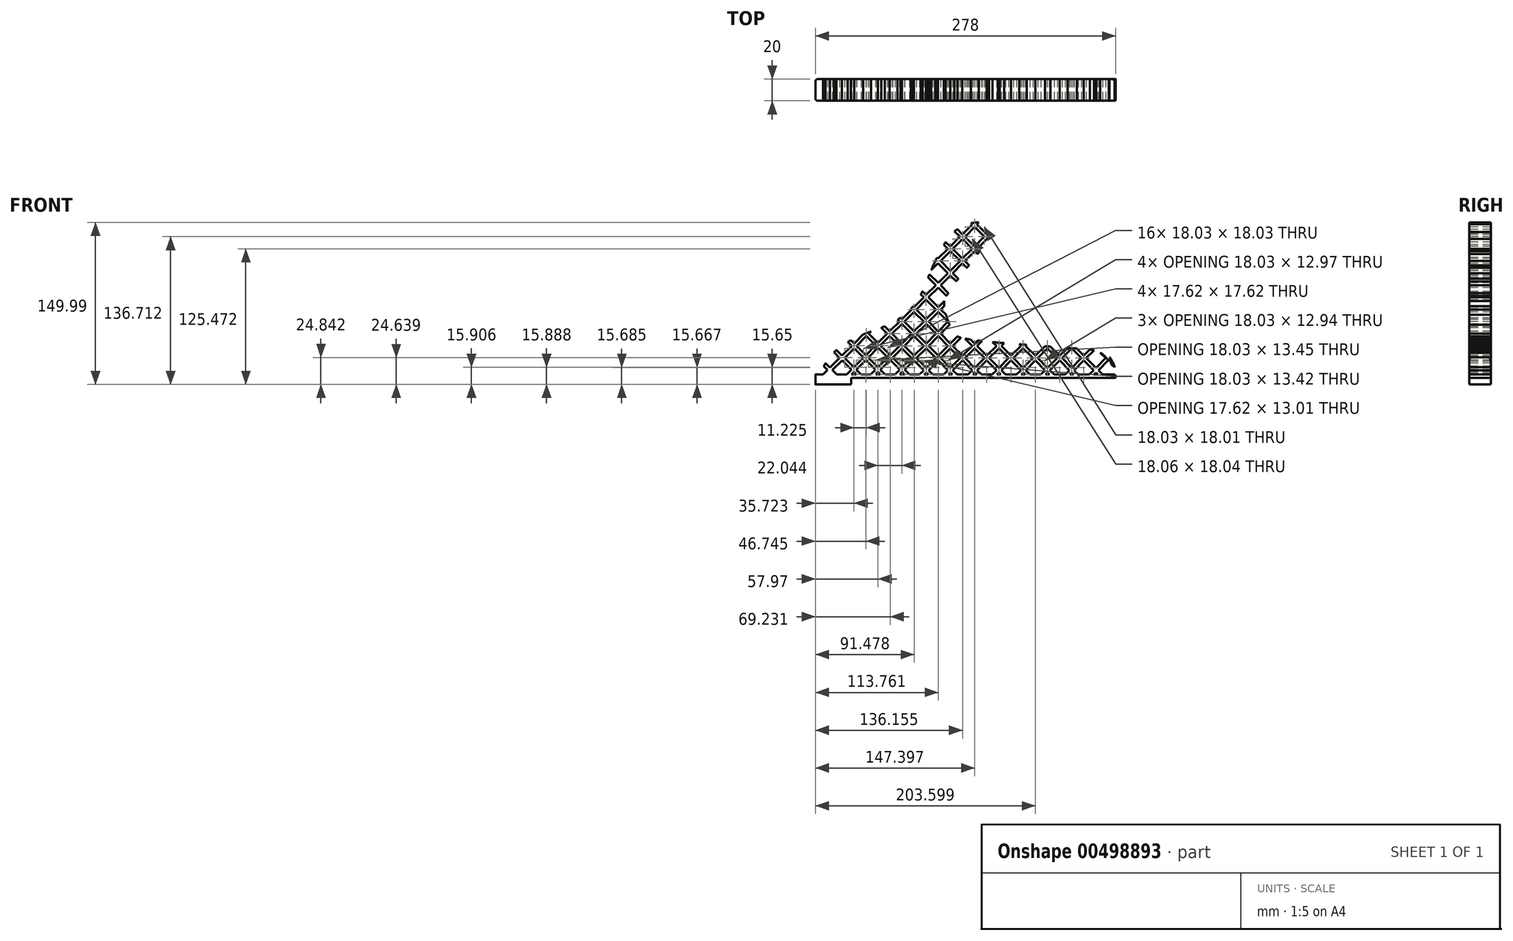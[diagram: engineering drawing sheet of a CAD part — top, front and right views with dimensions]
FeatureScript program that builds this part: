
annotation { "Feature Type Name" : "Feature", "Feature Type Description" : "" }
export const myFeature = defineFeature(function(context is Context, id is Id, definition is map)
    precondition{}
    {
        {
            var Q0;
            Q0=qCreatedBy(makeId("Front.planeOp"),FACE);
            var sketch = newSketch(context, id + "F0", { "sketchPlane" : qUnion([Q0])});
            skLineSegment(sketch, "E0", {"start": v(-83, -3.17) * mm, "end": v(-83, 0) * mm});
            skLineSegment(sketch, "E1", {"start": v(-83, 0) * mm, "end": v(-82.7, 0) * mm});
            skArc(sketch, "E2", {"start": v(162, 0) * mm, "mid": v(155.8, 16.5) * mm, "end": v(140.24, 24.79) * mm});
            skLineSegment(sketch, "E3", {"start": v(140.24, 24.79) * mm, "end": v(39.58, 33.6) * mm});
            skFitSpline(sketch, "E4", {"points": [v(-116, 0) * mm, v(-106.77, 17.97) * mm, v(-86.19, 34.74) * mm, v(-51.87, 47.68) * mm, v(-30.13, 63.36) * mm, v(-15.89, 87.59) * mm, v(-3.25, 115.08) * mm, v(10.46, 133.67) * mm, v(27.88, 142.86) * mm, v(45.91, 140.16) * mm, v(44.88, 124.4) * mm, v(32.37, 105.05) * mm, v(24.04, 94.4) * mm, v(12.3, 78.31) * mm], "startDerivative": vector(110.14, 372.48) * mm, "endDerivative": vector(-175.67, -307.4) * mm});
            skFitSpline(sketch, "E5", {"points": [v(-110.58, 0) * mm, v(-109.72, 3.92) * mm, v(-104.27, 14.22) * mm, v(-97.47, 21.84) * mm, v(-91.58, 26.62) * mm, v(-79.54, 33.6) * mm, v(-68.24, 38.4) * mm, v(-52.26, 44.4) * mm, v(-40.42, 50.4) * mm, v(-31.67, 56.73) * mm, v(-26.67, 61.88) * mm, v(-19.12, 72.72) * mm, v(-10.73, 92.02) * mm, v(-2.47, 110.27) * mm, v(4.52, 122.74) * mm, v(11.8, 131.72) * mm, v(18.12, 135.9) * mm, v(25.92, 139.48) * mm, v(34.7, 140.8) * mm, v(38.92, 140.55) * mm, v(43.31, 138.54) * mm, v(44.78, 133) * mm, v(42.07, 124.02) * mm, v(36.65, 115) * mm, v(29.24, 104.7) * mm, v(18.05, 91.14) * mm, v(10.55, 80.15) * mm, v(5.27, 72.64) * mm, v(3.17, 63.32) * mm, v(10.92, 40.34) * mm, v(22.95, 33.11) * mm, v(135.88, 23.55) * mm, v(145.48, 22.31) * mm, v(155.41, 17.66) * mm, v(158.63, 8.75) * mm, v(163.79, 4.17) * mm, v(158.83, 0) * mm], "startDerivative": vector(86.06, 309.75) * mm, "endDerivative": vector(-2.43, -186.75) * mm});
            skLineSegment(sketch, "E6", {"start": v(-100.7, 0) * mm, "end": v(-102.52, 1.82) * mm});
            skLineSegment(sketch, "E7", {"start": v(-96.29, 0) * mm, "end": v(-100.32, 4.03) * mm});
            skLineSegment(sketch, "E8", {"start": v(-98.81, 20.56) * mm, "end": v(-93.54, 15.3) * mm});
            skLineSegment(sketch, "E9", {"start": v(-96.53, 22.7) * mm, "end": v(-91.33, 17.5) * mm});
            skLineSegment(sketch, "E10", {"start": v(-85.94, 30.14) * mm, "end": v(-82.32, 26.52) * mm});
            skLineSegment(sketch, "E11", {"start": v(-83.11, 31.73) * mm, "end": v(-80.1, 28.73) * mm});
            skLineSegment(sketch, "E12", {"start": v(-68.85, 35.5) * mm, "end": v(-60.24, 26.89) * mm});
            skLineSegment(sketch, "E13", {"start": v(-28.93, 0) * mm, "end": v(-33.33, 4.4) * mm});
            skLineSegment(sketch, "E14", {"start": v(-55.01, 43.3) * mm, "end": v(-49.42, 37.7) * mm});
            skLineSegment(sketch, "E15", {"start": v(-51.87, 44.57) * mm, "end": v(-47.21, 39.92) * mm});
            skLineSegment(sketch, "E16", {"start": v(-39.95, 50.68) * mm, "end": v(-38.2, 48.93) * mm});
            skLineSegment(sketch, "E17", {"start": v(-37.28, 52.44) * mm, "end": v(-35.99, 51.14) * mm});
            skLineSegment(sketch, "E18", {"start": v(-27.6, 60.79) * mm, "end": v(-26.97, 60.16) * mm});
            skLineSegment(sketch, "E19", {"start": v(-25.58, 63.2) * mm, "end": v(-24.76, 62.37) * mm});
            skLineSegment(sketch, "E20", {"start": v(-18.42, 74.05) * mm, "end": v(-15.75, 71.38) * mm});
            skLineSegment(sketch, "E21", {"start": v(-16.97, 77.02) * mm, "end": v(-13.54, 73.6) * mm});
            skLineSegment(sketch, "E22", {"start": v(-11.66, 89.75) * mm, "end": v(-4.52, 82.6) * mm});
            skLineSegment(sketch, "E23", {"start": v(-10.38, 92.89) * mm, "end": v(-2.31, 84.82) * mm});
            skLineSegment(sketch, "E24", {"start": v(-4.84, 105.38) * mm, "end": v(-4.6, 105.15) * mm});
            skLineSegment(sketch, "E25", {"start": v(-3.4, 108.36) * mm, "end": v(-2.4, 107.36) * mm});
            skLineSegment(sketch, "E26", {"start": v(31.39, 114.1) * mm, "end": v(34.18, 111.35) * mm});
            skLineSegment(sketch, "E27", {"start": v(33.6, 116.3) * mm, "end": v(35.96, 113.98) * mm});
            skLineSegment(sketch, "E28", {"start": v(40.41, 127.54) * mm, "end": v(31.38, 136.54) * mm});
            skLineSegment(sketch, "E29", {"start": v(42.62, 129.75) * mm, "end": v(33.32, 139.01) * mm});
            skLineSegment(sketch, "E30", {"start": v(121.27, 24.16) * mm, "end": v(130.3, 15.15) * mm});
            skLineSegment(sketch, "E31", {"start": v(125.87, 24) * mm, "end": v(132.5, 17.36) * mm});
            skLineSegment(sketch, "E32.trimOffspring", {"start": v(101.57, 25.84) * mm, "end": v(110.05, 17.36) * mm});
            skLineSegment(sketch, "E33.trimOffspring", {"start": v(98.82, 24.16) * mm, "end": v(107.84, 15.15) * mm});
            skLineSegment(sketch, "E34.trimOffspring", {"start": v(78.55, 26.4) * mm, "end": v(87.56, 17.4) * mm});
            skLineSegment(sketch, "E35.trimOffspring", {"start": v(72.62, 27.92) * mm, "end": v(74.13, 26.4) * mm});
            skLineSegment(sketch, "E36.trimOffspring", {"start": v(52.95, 29.56) * mm, "end": v(53.77, 28.74) * mm});
            skLineSegment(sketch, "E37.trimOffspring", {"start": v(48.08, 30) * mm, "end": v(51.68, 26.4) * mm});
            skLineSegment(sketch, "E38", {"start": v(-104.34, 0) * mm, "end": v(-102.52, 1.82) * mm});
            skLineSegment(sketch, "E39", {"start": v(-108.83, 0) * mm, "end": v(-104.77, 4.07) * mm});
            skLineSegment(sketch, "E40", {"start": v(-87.13, 0) * mm, "end": v(-82.7, 4.44) * mm});
            skLineSegment(sketch, "E41.trimOffspring", {"start": v(42.62, 129.75) * mm, "end": v(44.65, 131.77) * mm});
            skLineSegment(sketch, "E42", {"start": v(-82.7, 0) * mm, "end": v(-80.48, 2.23) * mm});
            skLineSegment(sketch, "E43", {"start": v(-5.25, 104.5) * mm, "end": v(-4.6, 105.15) * mm});
            skLineSegment(sketch, "E44", {"start": v(20.08, 129.63) * mm, "end": v(29.08, 138.66) * mm});
            skLineSegment(sketch, "E45.trimOffspring", {"start": v(29.08, 138.66) * mm, "end": v(27.78, 139.96) * mm});
            skLineSegment(sketch, "E46.trimOffspring", {"start": v(33.32, 139.01) * mm, "end": v(35.11, 140.81) * mm});
            skLineSegment(sketch, "E47", {"start": v(-60.19, 0) * mm, "end": v(-58, 2.2) * mm});
            skLineSegment(sketch, "E48", {"start": v(-64.68, 0) * mm, "end": v(-60.24, 4.44) * mm});
            skLineSegment(sketch, "E49", {"start": v(-42.15, 0) * mm, "end": v(-37.75, 4.4) * mm});
            skLineSegment(sketch, "E50", {"start": v(-37.74, 0) * mm, "end": v(-35.54, 2.2) * mm});
            skLineSegment(sketch, "E51", {"start": v(-15.21, 0) * mm, "end": v(-13.46, 1.75) * mm});
            skLineSegment(sketch, "E52", {"start": v(-19.7, 0) * mm, "end": v(-15.7, 4) * mm});
            skLineSegment(sketch, "E53", {"start": v(2.82, 0) * mm, "end": v(6.78, 3.96) * mm});
            skLineSegment(sketch, "E54", {"start": v(7.24, 0) * mm, "end": v(8.99, 1.75) * mm});
            skLineSegment(sketch, "E55", {"start": v(29.69, 0) * mm, "end": v(31.44, 1.75) * mm});
            skLineSegment(sketch, "E56", {"start": v(25.27, 0) * mm, "end": v(29.23, 3.96) * mm});
            skLineSegment(sketch, "E57", {"start": v(47.72, 0) * mm, "end": v(51.68, 3.96) * mm});
            skLineSegment(sketch, "E58", {"start": v(52.14, 0) * mm, "end": v(53.89, 1.75) * mm});
            skLineSegment(sketch, "E59", {"start": v(74.66, 0) * mm, "end": v(76.37, 1.71) * mm});
            skLineSegment(sketch, "E60", {"start": v(70.17, 0) * mm, "end": v(74.13, 3.96) * mm});
            skLineSegment(sketch, "E61", {"start": v(92.7, 0) * mm, "end": v(96.61, 3.92) * mm});
            skLineSegment(sketch, "E62", {"start": v(97.1, 0) * mm, "end": v(98.82, 1.71) * mm});
            skLineSegment(sketch, "E63", {"start": v(119.56, 0) * mm, "end": v(121.27, 1.71) * mm});
            skLineSegment(sketch, "E64", {"start": v(115.14, 0) * mm, "end": v(119.06, 3.92) * mm});
            skLineSegment(sketch, "E65", {"start": v(137.6, 0) * mm, "end": v(141.52, 3.92) * mm});
            skLineSegment(sketch, "E66", {"start": v(142.01, 0) * mm, "end": v(143.73, 1.71) * mm});
            skPoint(sketch, "E67.orphan", {"position": v(103.07, -34.52) * mm});
            skPoint(sketch, "E68.orphan", {"position": v(85.04, -34.52) * mm});
            skPoint(sketch, "E69.orphan", {"position": v(0, -2.82) * mm});
            skLineSegment(sketch, "E70", {"start": v(-83, 0) * mm, "end": v(-100.7, 0) * mm});
            skLineSegment(sketch, "E71.trimOffspring", {"start": v(-104.77, 4.07) * mm, "end": v(-108.22, 7.52) * mm});
            skLineSegment(sketch, "E72.trimOffspring", {"start": v(-102.56, 6.27) * mm, "end": v(-93.54, 15.3) * mm});
            skLineSegment(sketch, "E73.trimOffspring", {"start": v(-102.56, 6.27) * mm, "end": v(-106.68, 10.4) * mm});
            skLineSegment(sketch, "E74.trimOffspring", {"start": v(-100.32, 4.03) * mm, "end": v(-91.3, 13.05) * mm});
            skLineSegment(sketch, "E75.trimOffspring", {"start": v(-91.3, 13.05) * mm, "end": v(-82.7, 4.44) * mm});
            skLineSegment(sketch, "E76.trimOffspring", {"start": v(-89.09, 15.26) * mm, "end": v(-80.48, 6.65) * mm});
            skLineSegment(sketch, "E77.trimOffspring", {"start": v(-91.33, 17.5) * mm, "end": v(-82.32, 26.52) * mm});
            skLineSegment(sketch, "E78.trimOffspring", {"start": v(-89.09, 15.26) * mm, "end": v(-80.07, 24.27) * mm});
            skLineSegment(sketch, "E79.trimOffspring", {"start": v(-80.48, 6.65) * mm, "end": v(-71.47, 15.66) * mm});
            skLineSegment(sketch, "E80.trimOffspring", {"start": v(-78.27, 4.44) * mm, "end": v(-69.26, 13.45) * mm});
            skLineSegment(sketch, "E81.trimOffspring", {"start": v(-78.27, 4.44) * mm, "end": v(-73.83, 0) * mm});
            skLineSegment(sketch, "E82.trimOffspring", {"start": v(-80.48, 2.23) * mm, "end": v(-78.25, 0) * mm});
            skLineSegment(sketch, "E83.trimOffspring", {"start": v(-80.07, 24.27) * mm, "end": v(-71.47, 15.66) * mm});
            skLineSegment(sketch, "E84.trimOffspring", {"start": v(-77.86, 26.48) * mm, "end": v(-69.26, 17.87) * mm});
            skLineSegment(sketch, "E85.trimOffspring", {"start": v(-80.1, 28.73) * mm, "end": v(-71.8, 37.04) * mm});
            skLineSegment(sketch, "E86.trimOffspring", {"start": v(-77.86, 26.48) * mm, "end": v(-68.85, 35.5) * mm});
            skLineSegment(sketch, "E87.trimOffspring", {"start": v(-69.26, 17.87) * mm, "end": v(-60.24, 26.89) * mm});
            skLineSegment(sketch, "E88.trimOffspring", {"start": v(-67.05, 15.66) * mm, "end": v(-58.03, 24.68) * mm});
            skLineSegment(sketch, "E89.trimOffspring", {"start": v(-67.05, 15.66) * mm, "end": v(-58.03, 6.65) * mm});
            skLineSegment(sketch, "E90.trimOffspring", {"start": v(-69.26, 13.45) * mm, "end": v(-60.24, 4.44) * mm});
            skLineSegment(sketch, "E91.trimOffspring", {"start": v(-58, 2.2) * mm, "end": v(-55.8, 0) * mm});
            skLineSegment(sketch, "E92.trimOffspring", {"start": v(-58.03, 6.65) * mm, "end": v(-49.01, 15.66) * mm});
            skLineSegment(sketch, "E93.trimOffspring", {"start": v(-55.78, 4.4) * mm, "end": v(-51.38, 0) * mm});
            skLineSegment(sketch, "E94.trimOffspring", {"start": v(-55.78, 4.4) * mm, "end": v(-46.77, 13.42) * mm});
            skLineSegment(sketch, "E95.trimOffspring", {"start": v(-66.64, 37.7) * mm, "end": v(-64.61, 39.73) * mm});
            skLineSegment(sketch, "E96.trimOffspring", {"start": v(-58.03, 29.1) * mm, "end": v(-49.42, 37.7) * mm});
            skLineSegment(sketch, "E97.trimOffspring", {"start": v(-55.82, 26.89) * mm, "end": v(-47.21, 35.5) * mm});
            skLineSegment(sketch, "E98.trimOffspring", {"start": v(-58.03, 29.1) * mm, "end": v(-66.64, 37.7) * mm});
            skLineSegment(sketch, "E99.trimOffspring", {"start": v(-58.03, 24.68) * mm, "end": v(-49.01, 15.66) * mm});
            skLineSegment(sketch, "E100.trimOffspring", {"start": v(-46.8, 17.87) * mm, "end": v(-38.2, 26.48) * mm});
            skLineSegment(sketch, "E101.trimOffspring", {"start": v(-44.56, 15.63) * mm, "end": v(-35.95, 24.24) * mm});
            skLineSegment(sketch, "E102.trimOffspring", {"start": v(-46.8, 17.87) * mm, "end": v(-55.82, 26.89) * mm});
            skLineSegment(sketch, "E103.trimOffspring", {"start": v(-46.77, 13.42) * mm, "end": v(-37.75, 4.4) * mm});
            skLineSegment(sketch, "E104.trimOffspring", {"start": v(-47.21, 39.92) * mm, "end": v(-38.2, 48.93) * mm});
            skLineSegment(sketch, "E105.trimOffspring", {"start": v(-45, 37.7) * mm, "end": v(-35.99, 28.7) * mm});
            skLineSegment(sketch, "E106.trimOffspring", {"start": v(-47.21, 35.5) * mm, "end": v(-38.2, 26.48) * mm});
            skLineSegment(sketch, "E107.trimOffspring", {"start": v(-45, 37.7) * mm, "end": v(-35.99, 46.72) * mm});
            skLineSegment(sketch, "E108.trimOffspring", {"start": v(-35.99, 28.7) * mm, "end": v(-26.97, 37.7) * mm});
            skLineSegment(sketch, "E109.trimOffspring", {"start": v(-33.74, 26.45) * mm, "end": v(-24.73, 35.46) * mm});
            skLineSegment(sketch, "E110.trimOffspring", {"start": v(-33.74, 26.45) * mm, "end": v(-24.73, 17.43) * mm});
            skLineSegment(sketch, "E111.trimOffspring", {"start": v(-35.95, 24.24) * mm, "end": v(-26.94, 15.22) * mm});
            skLineSegment(sketch, "E112.trimOffspring", {"start": v(-35.99, 46.72) * mm, "end": v(-26.97, 37.7) * mm});
            skLineSegment(sketch, "E113.trimOffspring", {"start": v(-35.99, 51.14) * mm, "end": v(-26.97, 60.16) * mm});
            skLineSegment(sketch, "E114.trimOffspring", {"start": v(-33.78, 48.93) * mm, "end": v(-24.76, 39.92) * mm});
            skLineSegment(sketch, "E115.trimOffspring", {"start": v(-33.78, 48.93) * mm, "end": v(-24.76, 57.95) * mm});
            skLineSegment(sketch, "E116.trimOffspring", {"start": v(-24.76, 39.92) * mm, "end": v(-15.75, 48.93) * mm});
            skLineSegment(sketch, "E117.trimOffspring", {"start": v(-22.52, 37.67) * mm, "end": v(-13.5, 46.69) * mm});
            skLineSegment(sketch, "E118.trimOffspring", {"start": v(-22.52, 37.67) * mm, "end": v(-13.5, 28.65) * mm});
            skLineSegment(sketch, "E119.trimOffspring", {"start": v(-24.73, 35.46) * mm, "end": v(-15.7, 26.45) * mm});
            skLineSegment(sketch, "E120.trimOffspring", {"start": v(-24.73, 17.43) * mm, "end": v(-15.7, 26.45) * mm});
            skLineSegment(sketch, "E121.trimOffspring", {"start": v(-22.52, 15.22) * mm, "end": v(-13.5, 24.24) * mm});
            skLineSegment(sketch, "E122.trimOffspring", {"start": v(-22.52, 15.22) * mm, "end": v(-13.5, 6.2) * mm});
            skLineSegment(sketch, "E123.trimOffspring", {"start": v(-24.73, 13.01) * mm, "end": v(-15.7, 4) * mm});
            skLineSegment(sketch, "E124.trimOffspring", {"start": v(-35.54, 6.61) * mm, "end": v(-44.56, 15.63) * mm});
            skLineSegment(sketch, "E125.trimOffspring", {"start": v(-35.54, 6.61) * mm, "end": v(-26.94, 15.22) * mm});
            skLineSegment(sketch, "E126.trimOffspring", {"start": v(-35.54, 2.2) * mm, "end": v(-33.35, 0) * mm});
            skLineSegment(sketch, "E127.trimOffspring", {"start": v(-33.33, 4.4) * mm, "end": v(-24.73, 13.01) * mm});
            skLineSegment(sketch, "E128.trimOffspring", {"start": v(-13.5, 6.2) * mm, "end": v(-4.48, 15.22) * mm});
            skLineSegment(sketch, "E129.trimOffspring", {"start": v(-11.25, 3.96) * mm, "end": v(-2.24, 12.97) * mm});
            skLineSegment(sketch, "E130.trimOffspring", {"start": v(-13.46, 1.75) * mm, "end": v(-11.72, 0) * mm});
            skLineSegment(sketch, "E131.trimOffspring", {"start": v(-11.25, 3.96) * mm, "end": v(-7.3, 0) * mm});
            skLineSegment(sketch, "E132.trimOffspring", {"start": v(-2.27, 17.43) * mm, "end": v(6.74, 26.45) * mm});
            skLineSegment(sketch, "E133.trimOffspring", {"start": v(-0.03, 15.18) * mm, "end": v(8.99, 24.2) * mm});
            skLineSegment(sketch, "E134.trimOffspring", {"start": v(-2.24, 12.97) * mm, "end": v(6.78, 3.96) * mm});
            skLineSegment(sketch, "E135.trimOffspring", {"start": v(-0.03, 15.18) * mm, "end": v(8.99, 6.17) * mm});
            skLineSegment(sketch, "E136.trimOffspring", {"start": v(-11.3, 26.45) * mm, "end": v(-2.27, 17.43) * mm});
            skLineSegment(sketch, "E137.trimOffspring", {"start": v(-13.5, 24.24) * mm, "end": v(-4.48, 15.22) * mm});
            skLineSegment(sketch, "E138.trimOffspring", {"start": v(-13.5, 28.65) * mm, "end": v(-4.48, 37.67) * mm});
            skLineSegment(sketch, "E139.trimOffspring", {"start": v(-11.3, 26.45) * mm, "end": v(-2.27, 35.46) * mm});
            skLineSegment(sketch, "E140.trimOffspring", {"start": v(-24.76, 57.95) * mm, "end": v(-15.75, 48.93) * mm});
            skLineSegment(sketch, "E141.trimOffspring", {"start": v(-24.76, 62.37) * mm, "end": v(-15.75, 71.38) * mm});
            skLineSegment(sketch, "E142.trimOffspring", {"start": v(-22.55, 60.16) * mm, "end": v(-13.54, 51.14) * mm});
            skLineSegment(sketch, "E143.trimOffspring", {"start": v(-22.55, 60.16) * mm, "end": v(-13.54, 69.17) * mm});
            skLineSegment(sketch, "E144.trimOffspring", {"start": v(-13.54, 69.17) * mm, "end": v(-4.52, 60.16) * mm});
            skLineSegment(sketch, "E145.trimOffspring", {"start": v(-13.54, 73.6) * mm, "end": v(-4.52, 82.6) * mm});
            skLineSegment(sketch, "E146.trimOffspring", {"start": v(-11.33, 71.38) * mm, "end": v(-2.27, 62.33) * mm});
            skLineSegment(sketch, "E147.trimOffspring", {"start": v(-11.33, 71.38) * mm, "end": v(-2.31, 80.4) * mm});
            skLineSegment(sketch, "E148.trimOffspring", {"start": v(-0.06, 60.12) * mm, "end": v(8.95, 69.14) * mm});
            skLineSegment(sketch, "E149.trimOffspring", {"start": v(-2.27, 57.91) * mm, "end": v(6.74, 48.9) * mm});
            skLineSegment(sketch, "E150.trimOffspring", {"start": v(-11.3, 48.9) * mm, "end": v(-2.27, 39.88) * mm});
            skLineSegment(sketch, "E151.trimOffspring", {"start": v(-13.54, 51.14) * mm, "end": v(-4.52, 60.16) * mm});
            skLineSegment(sketch, "E152.trimOffspring", {"start": v(-13.5, 46.69) * mm, "end": v(-4.48, 37.67) * mm});
            skLineSegment(sketch, "E153.trimOffspring", {"start": v(-11.3, 48.9) * mm, "end": v(-2.27, 57.91) * mm});
            skLineSegment(sketch, "E154.trimOffspring", {"start": v(-2.27, 39.88) * mm, "end": v(6.74, 48.9) * mm});
            skLineSegment(sketch, "E155.trimOffspring", {"start": v(-0.06, 37.67) * mm, "end": v(8.99, 28.62) * mm});
            skLineSegment(sketch, "E156.trimOffspring", {"start": v(-2.27, 35.46) * mm, "end": v(6.74, 26.45) * mm});
            skLineSegment(sketch, "E157.trimOffspring", {"start": v(22.5, 15.27) * mm, "end": v(31.44, 24.2) * mm});
            skLineSegment(sketch, "E158.trimOffspring", {"start": v(8.99, 24.2) * mm, "end": v(18, 15.18) * mm});
            skLineSegment(sketch, "E159.trimOffspring", {"start": v(20.21, 12.97) * mm, "end": v(29.23, 3.96) * mm});
            skLineSegment(sketch, "E160.trimOffspring", {"start": v(22.42, 15.18) * mm, "end": v(31.44, 6.17) * mm});
            skLineSegment(sketch, "E161.trimOffspring", {"start": v(20.21, 17.4) * mm, "end": v(29.23, 26.4) * mm});
            skLineSegment(sketch, "E162.trimOffspring", {"start": v(22.42, 15.18) * mm, "end": v(31.44, 24.2) * mm});
            skLineSegment(sketch, "E163.trimOffspring", {"start": v(31.44, 24.2) * mm, "end": v(40.45, 15.18) * mm});
            skLineSegment(sketch, "E164.trimOffspring", {"start": v(33.65, 26.4) * mm, "end": v(42.66, 17.4) * mm});
            skLineSegment(sketch, "E165.trimOffspring", {"start": v(33.65, 26.4) * mm, "end": v(38.25, 31.02) * mm});
            skLineSegment(sketch, "E166.trimOffspring", {"start": v(44.87, 15.18) * mm, "end": v(53.89, 6.17) * mm});
            skLineSegment(sketch, "E167.trimOffspring", {"start": v(42.66, 12.97) * mm, "end": v(51.68, 3.96) * mm});
            skLineSegment(sketch, "E168.trimOffspring", {"start": v(44.87, 15.18) * mm, "end": v(53.89, 24.2) * mm});
            skLineSegment(sketch, "E169.trimOffspring", {"start": v(53.89, 24.2) * mm, "end": v(62.9, 15.18) * mm});
            skLineSegment(sketch, "E170.trimOffspring", {"start": v(56.1, 26.4) * mm, "end": v(65.11, 17.4) * mm});
            skLineSegment(sketch, "E171.trimOffspring", {"start": v(53.77, 28.74) * mm, "end": v(54.45, 29.42) * mm});
            skLineSegment(sketch, "E172.trimOffspring", {"start": v(56.1, 26.4) * mm, "end": v(58.73, 29.05) * mm});
            skLineSegment(sketch, "E173.trimOffspring", {"start": v(56.1, 3.96) * mm, "end": v(60.06, 0) * mm});
            skLineSegment(sketch, "E174.trimOffspring", {"start": v(53.89, 6.17) * mm, "end": v(62.9, 15.18) * mm});
            skLineSegment(sketch, "E175.trimOffspring", {"start": v(53.89, 1.75) * mm, "end": v(55.64, 0) * mm});
            skLineSegment(sketch, "E176.trimOffspring", {"start": v(56.1, 3.96) * mm, "end": v(65.11, 12.97) * mm});
            skLineSegment(sketch, "E177.trimOffspring", {"start": v(65.11, 17.4) * mm, "end": v(74.13, 26.4) * mm});
            skLineSegment(sketch, "E178.trimOffspring", {"start": v(67.32, 15.18) * mm, "end": v(76.34, 6.17) * mm});
            skLineSegment(sketch, "E179.trimOffspring", {"start": v(67.32, 15.18) * mm, "end": v(76.34, 24.2) * mm});
            skLineSegment(sketch, "E180.trimOffspring", {"start": v(65.11, 12.97) * mm, "end": v(74.13, 3.96) * mm});
            skLineSegment(sketch, "E181.trimOffspring", {"start": v(76.34, 6.17) * mm, "end": v(85.35, 15.18) * mm});
            skLineSegment(sketch, "E182.trimOffspring", {"start": v(78.58, 3.92) * mm, "end": v(82.5, 0) * mm});
            skLineSegment(sketch, "E183.trimOffspring", {"start": v(76.37, 1.71) * mm, "end": v(78.09, 0) * mm});
            skLineSegment(sketch, "E184.trimOffspring", {"start": v(78.58, 3.92) * mm, "end": v(87.6, 12.94) * mm});
            skLineSegment(sketch, "E185.trimOffspring", {"start": v(87.6, 12.94) * mm, "end": v(96.61, 3.92) * mm});
            skLineSegment(sketch, "E186.trimOffspring", {"start": v(78.55, 26.4) * mm, "end": v(79.53, 27.4) * mm});
            skLineSegment(sketch, "E187.trimOffspring", {"start": v(76.34, 24.2) * mm, "end": v(85.35, 15.18) * mm});
            skLineSegment(sketch, "E188.trimOffspring", {"start": v(89.8, 15.15) * mm, "end": v(98.82, 24.16) * mm});
            skLineSegment(sketch, "E189.trimOffspring", {"start": v(89.8, 15.15) * mm, "end": v(98.82, 6.13) * mm});
            skLineSegment(sketch, "E190.trimOffspring", {"start": v(87.56, 17.4) * mm, "end": v(96.36, 26.2) * mm});
            skLineSegment(sketch, "E191.trimOffspring", {"start": v(110.05, 17.36) * mm, "end": v(117.32, 24.63) * mm});
            skLineSegment(sketch, "E192.trimOffspring", {"start": v(112.26, 15.15) * mm, "end": v(121.27, 6.13) * mm});
            skLineSegment(sketch, "E193.trimOffspring", {"start": v(112.26, 15.15) * mm, "end": v(121.27, 24.16) * mm});
            skLineSegment(sketch, "E194.trimOffspring", {"start": v(110.05, 12.94) * mm, "end": v(119.06, 3.92) * mm});
            skLineSegment(sketch, "E195.trimOffspring", {"start": v(101.03, 3.92) * mm, "end": v(104.96, 0) * mm});
            skLineSegment(sketch, "E196.trimOffspring", {"start": v(98.82, 6.13) * mm, "end": v(107.84, 15.15) * mm});
            skLineSegment(sketch, "E197.trimOffspring", {"start": v(98.82, 1.71) * mm, "end": v(100.54, 0) * mm});
            skLineSegment(sketch, "E198.trimOffspring", {"start": v(101.03, 3.92) * mm, "end": v(110.05, 12.94) * mm});
            skLineSegment(sketch, "E199.trimOffspring", {"start": v(132.5, 17.36) * mm, "end": v(138.23, 23.1) * mm});
            skLineSegment(sketch, "E200.trimOffspring", {"start": v(134.7, 15.15) * mm, "end": v(141.93, 22.37) * mm});
            skLineSegment(sketch, "E201.trimOffspring", {"start": v(134.7, 15.15) * mm, "end": v(143.73, 6.13) * mm});
            skLineSegment(sketch, "E202.trimOffspring", {"start": v(132.5, 12.94) * mm, "end": v(141.52, 3.92) * mm});
            skLineSegment(sketch, "E203.trimOffspring", {"start": v(123.48, 3.92) * mm, "end": v(127.4, 0) * mm});
            skLineSegment(sketch, "E204.trimOffspring", {"start": v(121.27, 1.71) * mm, "end": v(122.99, 0) * mm});
            skLineSegment(sketch, "E205.trimOffspring", {"start": v(121.27, 6.13) * mm, "end": v(130.3, 15.15) * mm});
            skLineSegment(sketch, "E206.trimOffspring", {"start": v(123.48, 3.92) * mm, "end": v(132.5, 12.94) * mm});
            skLineSegment(sketch, "E207.trimOffspring", {"start": v(143.73, 6.13) * mm, "end": v(152.74, 15.15) * mm});
            skLineSegment(sketch, "E208.trimOffspring", {"start": v(145.93, 3.92) * mm, "end": v(154.95, 12.94) * mm});
            skLineSegment(sketch, "E209.trimOffspring", {"start": v(145.93, 3.92) * mm, "end": v(149.86, 0) * mm});
            skLineSegment(sketch, "E210.trimOffspring", {"start": v(143.73, 1.71) * mm, "end": v(145.44, 0) * mm});
            skLineSegment(sketch, "E211.trimOffspring", {"start": v(-2.31, 84.82) * mm, "end": v(6.7, 93.83) * mm});
            skLineSegment(sketch, "E212.trimOffspring", {"start": v(-0.1, 82.6) * mm, "end": v(8.92, 91.62) * mm});
            skLineSegment(sketch, "E213.trimOffspring", {"start": v(-2.4, 107.36) * mm, "end": v(6.54, 116.3) * mm});
            skLineSegment(sketch, "E214.trimOffspring", {"start": v(-2.4, 102.94) * mm, "end": v(6.7, 93.83) * mm});
            skLineSegment(sketch, "E215.trimOffspring", {"start": v(-0.1, 105.06) * mm, "end": v(8.91, 114.08) * mm});
            skLineSegment(sketch, "E216.trimOffspring", {"start": v(6.54, 116.3) * mm, "end": v(2.82, 120.02) * mm});
            skLineSegment(sketch, "E217.trimOffspring", {"start": v(8.75, 118.5) * mm, "end": v(17.77, 127.52) * mm});
            skLineSegment(sketch, "E218.trimOffspring", {"start": v(8.75, 118.5) * mm, "end": v(4.52, 122.74) * mm});
            skLineSegment(sketch, "E219.trimOffspring", {"start": v(11.12, 116.29) * mm, "end": v(20.15, 125.31) * mm});
            skLineSegment(sketch, "E220.trimOffspring", {"start": v(17.93, 105.06) * mm, "end": v(8.91, 114.08) * mm});
            skLineSegment(sketch, "E221.trimOffspring", {"start": v(22.37, 105.08) * mm, "end": v(31.39, 114.1) * mm});
            skLineSegment(sketch, "E222.trimOffspring", {"start": v(20.14, 107.27) * mm, "end": v(11.12, 116.29) * mm});
            skLineSegment(sketch, "E223.trimOffspring", {"start": v(29.19, 116.32) * mm, "end": v(20.15, 125.31) * mm});
            skLineSegment(sketch, "E224.trimOffspring", {"start": v(31.4, 118.52) * mm, "end": v(22.38, 127.5) * mm});
            skLineSegment(sketch, "E225.trimOffspring", {"start": v(33.6, 116.3) * mm, "end": v(42.7, 125.42) * mm});
            skLineSegment(sketch, "E226.trimOffspring", {"start": v(31.4, 118.52) * mm, "end": v(40.41, 127.54) * mm});
            skLineSegment(sketch, "E227.trimOffspring", {"start": v(22.38, 127.5) * mm, "end": v(31.38, 136.54) * mm});
            skLineSegment(sketch, "E228.trimOffspring", {"start": v(17.77, 127.52) * mm, "end": v(12.76, 132.53) * mm});
            skLineSegment(sketch, "E229.trimOffspring", {"start": v(20.08, 129.63) * mm, "end": v(15.37, 134.34) * mm});
            skLineSegment(sketch, "E230.trimOffspring", {"start": v(20.14, 107.27) * mm, "end": v(29.19, 116.32) * mm});
            skLineSegment(sketch, "E231.trimOffspring", {"start": v(-104.34, 0) * mm, "end": v(-116, 0) * mm});
            skLineSegment(sketch, "E232.trimOffspring", {"start": v(-78.25, 0) * mm, "end": v(159.43, 0) * mm});
            skLineSegment(sketch, "E233", {"start": v(-82.7, 0) * mm, "end": v(-78.25, 0) * mm});
            skLineSegment(sketch, "E234.trimOffspring", {"start": v(31.44, 6.17) * mm, "end": v(40.45, 15.18) * mm});
            skLineSegment(sketch, "E235.trimOffspring", {"start": v(33.65, 3.96) * mm, "end": v(42.66, 12.97) * mm});
            skLineSegment(sketch, "E236.trimOffspring", {"start": v(31.44, 1.75) * mm, "end": v(33.19, 0) * mm});
            skLineSegment(sketch, "E237.trimOffspring", {"start": v(33.65, 3.96) * mm, "end": v(37.6, 0) * mm});
            skLineSegment(sketch, "E238.trimOffspring", {"start": v(11.2, 3.96) * mm, "end": v(15.15, 0) * mm});
            skLineSegment(sketch, "E239.trimOffspring", {"start": v(8.99, 6.17) * mm, "end": v(18, 15.18) * mm});
            skLineSegment(sketch, "E240.trimOffspring", {"start": v(8.99, 1.75) * mm, "end": v(10.74, 0) * mm});
            skLineSegment(sketch, "E241.trimOffspring", {"start": v(11.2, 3.96) * mm, "end": v(20.21, 12.97) * mm});
            skFitSpline(sketch, "E242", {"points": [v(39.58, 33.6) * mm, v(29.2, 36.2) * mm, v(24.64, 38.85) * mm, v(19.31, 45.16) * mm, v(16.43, 50.98) * mm, v(15.23, 59.34) * mm, v(15.57, 67.86) * mm, v(16.67, 75.73) * mm, v(18.02, 81.55) * mm, v(20.18, 87.66) * mm, v(24.04, 94.4) * mm], "startDerivative": vector(-99.51, 16.75) * mm, "endDerivative": vector(46.52, 71.35) * mm});
            skFitSpline(sketch, "E243", {"points": [v(38.25, 31.02) * mm, v(27.62, 33.52) * mm, v(22.42, 37.1) * mm, v(17.07, 43.11) * mm, v(14.09, 49.32) * mm, v(12.87, 58.46) * mm, v(12.92, 67) * mm, v(13.91, 74.62) * mm, v(15.42, 81.11) * mm, v(17.59, 88.06) * mm, v(21.9, 95.95) * mm], "startDerivative": vector(-99.47, 17.06) * mm, "endDerivative": vector(46.53, 71.34) * mm});
            skLineSegment(sketch, "E244", {"start": v(8.99, 28.62) * mm, "end": v(18, 37.64) * mm});
            skLineSegment(sketch, "E245", {"start": v(20.21, 17.4) * mm, "end": v(11.2, 26.4) * mm});
            skLineSegment(sketch, "E246", {"start": v(11.2, 26.4) * mm, "end": v(20.21, 35.43) * mm});
            skLineSegment(sketch, "E247", {"start": v(29.23, 26.4) * mm, "end": v(20.21, 35.43) * mm});
            skLineSegment(sketch, "E248", {"start": v(31.44, 28.62) * mm, "end": v(25.33, 34.73) * mm});
            skLineSegment(sketch, "E249", {"start": v(31.44, 28.62) * mm, "end": v(34.5, 31.68) * mm});
            skLineSegment(sketch, "E250", {"start": v(18, 37.64) * mm, "end": v(8.95, 46.69) * mm});
            skLineSegment(sketch, "E251", {"start": v(-0.06, 37.67) * mm, "end": v(8.95, 46.69) * mm});
            skLineSegment(sketch, "E252", {"start": v(17.41, 42.64) * mm, "end": v(11.16, 48.9) * mm});
            skLineSegment(sketch, "E253", {"start": v(8.95, 51.1) * mm, "end": v(13.1, 55.25) * mm});
            skLineSegment(sketch, "E254", {"start": v(11.16, 48.9) * mm, "end": v(13.62, 51.36) * mm});
            skLineSegment(sketch, "E255.trimOffspring", {"start": v(8.95, 51.1) * mm, "end": v(-0.06, 60.12) * mm});
            skPoint(sketch, "E256.orphan", {"position": v(6.74, 48.9) * mm});
            skLineSegment(sketch, "E257", {"start": v(-2.27, 62.33) * mm, "end": v(6.74, 71.35) * mm});
            skLineSegment(sketch, "E258", {"start": v(-2.31, 80.4) * mm, "end": v(6.74, 71.35) * mm});
            skLineSegment(sketch, "E259", {"start": v(-0.1, 82.6) * mm, "end": v(8.95, 73.56) * mm});
            skLineSegment(sketch, "E260.trimOffspring", {"start": v(8.95, 73.56) * mm, "end": v(15.05, 79.65) * mm});
            skLineSegment(sketch, "E261", {"start": v(8.95, 69.14) * mm, "end": v(12.83, 65.26) * mm});
            skLineSegment(sketch, "E262", {"start": v(11.16, 71.35) * mm, "end": v(13.13, 69.37) * mm});
            skLineSegment(sketch, "E263.trimOffspring", {"start": v(11.16, 71.35) * mm, "end": v(13.8, 73.98) * mm});
            skLineSegment(sketch, "E264", {"start": v(22.37, 105.08) * mm, "end": v(22.35, 105.06) * mm});
            skLineSegment(sketch, "E265", {"start": v(21.9, 95.95) * mm, "end": v(20.9, 94.39) * mm});
            skLineSegment(sketch, "E266", {"start": v(8.91, 96.04) * mm, "end": v(17.93, 105.06) * mm});
            skLineSegment(sketch, "E267", {"start": v(20.14, 102.85) * mm, "end": v(24.25, 98.74) * mm});
            skLineSegment(sketch, "E268", {"start": v(22.35, 105.06) * mm, "end": v(26.28, 101.12) * mm});
            skLineSegment(sketch, "E269.trimOffspring", {"start": v(20.14, 102.85) * mm, "end": v(11.12, 93.83) * mm});
            skLineSegment(sketch, "E270", {"start": v(8.91, 96.04) * mm, "end": v(-0.1, 105.06) * mm});
            skLineSegment(sketch, "E271", {"start": v(8.92, 91.62) * mm, "end": v(16.27, 84.27) * mm});
            skLineSegment(sketch, "E272", {"start": v(11.12, 93.83) * mm, "end": v(17.39, 87.57) * mm});
            skLineSegment(sketch, "E273", {"start": v(-2.4, 102.94) * mm, "end": v(-8.86, 96.47) * mm});
            skArc(sketch, "E274", {"start": v(159.43, 0) * mm, "mid": v(155.74, 12.08) * mm, "end": v(146.63, 20.82) * mm});
            skLineSegment(sketch, "E275", {"start": v(162, 0) * mm, "end": v(159.43, 0) * mm});
            skFitSpline(sketch, "E276", {"points": [v(146.63, 20.82) * mm, v(138.78, 23.01) * mm, v(129, 23.8) * mm, v(118.27, 24.55) * mm, v(101.57, 25.84) * mm], "startDerivative": vector(-35.56, 14.44) * mm, "endDerivative": vector(-70.12, 5.6) * mm});
            skLineSegment(sketch, "E277", {"start": v(152.74, 15.15) * mm, "end": v(147.72, 20.17) * mm});
            skLineSegment(sketch, "E278", {"start": v(154.95, 12.94) * mm, "end": v(155.63, 12.26) * mm});
            skLineSegment(sketch, "E279", {"start": v(51.68, 26.4) * mm, "end": v(42.66, 17.4) * mm});
            skLineSegment(sketch, "E280", {"start": v(-83, -3.17) * mm, "end": v(162, -3.17) * mm});
            skLineSegment(sketch, "E281", {"start": v(162, 0) * mm, "end": v(162, -3.17) * mm});
            skPoint(sketch, "E282.orphan", {"position": v(-83, -6.35) * mm});
            skLineSegment(sketch, "E283", {"start": v(-116, 0) * mm, "end": v(-116, -9.18) * mm});
            skLineSegment(sketch, "E284", {"start": v(-116, -9.18) * mm, "end": v(-83, -9.17) * mm});
            skLineSegment(sketch, "E285", {"start": v(-83, -9.17) * mm, "end": v(-83, -3.17) * mm});
            skSolve(sketch);
        }
        {
            var Q0;
            {var subQ46=sQuery(id+"F0.wireOp",EDGE,"E2");Q0=makeQuery(id+"F0.imprint","IMPRINT",FACE,{"disambiguationData":[TD([[makeQuery(id+"F0.imprint","IMPRINT",EDGE,{"derivedFrom":subQ46}),1.0]])]});}
            var Q1;
            {var subQ9=sQuery(id+"F0.wireOp",EDGE,"rZGNKk4H-3cCX-Ptvv-1g7i-rYawVHOiqHtw");Q1=makeQuery(id+"F0.imprint","IMPRINT",FACE,{"disambiguationData":[TD([[makeQuery(id+"F0.imprint","IMPRINT",EDGE,{"derivedFrom":subQ9}),1.0]])]});}
            var Q2;
            Q2=makeQuery(id+"F0.imprint","IMPRINT",FACE,{"disambiguationData":[TD([[makeQuery(id+"F0.imprint","IMPRINT",EDGE,{"derivedFrom":sQuery(id+"F0.wireOp",EDGE,"E0")}),-1.0]])]});
            var Q3;
            {var subQ9=sQuery(id+"F0.wireOp",EDGE,"E0");Q3=makeQuery(id+"F0.imprint","IMPRINT",FACE,{"disambiguationData":[TD([[makeQuery(id+"F0.imprint","IMPRINT",EDGE,{"derivedFrom":subQ9}),1.0]])]});}
            extrude(context, id + "F1", {"entities" : qUnion([Q0, Q1, Q2, Q3]), "oppositeDirection" : true, "depth" : 20 * mm});
        }
        {
            var Q0;
            {var subQ44=sQuery(id+"F0.wireOp",EDGE,"E1");Q0=makeQuery(id+"F0.imprint","IMPRINT",FACE,{"disambiguationData":[TD([[makeQuery(id+"F0.imprint","IMPRINT",EDGE,{"derivedFrom":subQ44}),1.0]])]});}
            extrude(context, id + "F2", {"entities" : qUnion([Q0]), "operationType" : NewBodyOperationType.ADD, "oppositeDirection" : true, "depth" : 20 * mm});
        }
        {
            var Q0;
            Q0=makeQuery(id+"F1.opExtrude","CAP_EDGE",EDGE,{"disambiguationData":[OSD([sQuery(id+"F0.wireOp",EDGE,"E2")])],"isStart":false});
            var Q1;
            Q1=makeQuery(id+"F1.opExtrude","CAP_EDGE",EDGE,{"disambiguationData":[OSD([sQuery(id+"F0.wireOp",EDGE,"E2")])],"isStart":true});
            var Q2;
            Q2=makeQuery(id+"F1.opExtrude","CAP_EDGE",EDGE,{"disambiguationData":[OSD([sQuery(id+"F0.wireOp",EDGE,"E3")])],"isStart":false});
            var Q3;
            Q3=makeQuery(id+"F1.opExtrude","CAP_EDGE",EDGE,{"disambiguationData":[OSD([sQuery(id+"F0.wireOp",EDGE,"E3")])],"isStart":true});
            var Q4;
            Q4=makeQuery(id+"F1.opExtrude","CAP_EDGE",EDGE,{"disambiguationData":[OSD([sQuery(id+"F0.wireOp",EDGE,"E242")])],"isStart":false});
            var Q5;
            Q5=makeQuery(id+"F1.opExtrude","CAP_EDGE",EDGE,{"disambiguationData":[OSD([sQuery(id+"F0.wireOp",EDGE,"E242")])],"isStart":true});
            var Q6;
            Q6=makeQuery(id+"F1.opExtrude","CAP_EDGE",EDGE,{"disambiguationData":[OSD([sQuery(id+"F0.wireOp",EDGE,"E4")])],"isStart":false});
            var Q7;
            Q7=makeQuery(id+"F1.opExtrude","CAP_EDGE",EDGE,{"disambiguationData":[OSD([sQuery(id+"F0.wireOp",EDGE,"E4")])],"isStart":true});
            var Q8;
            Q8=makeQuery(id+"F1.opExtrude","CAP_EDGE",EDGE,{"disambiguationData":[OSD([sQuery(id+"F0.wireOp",EDGE,"rZGNKk4H-3cCX-Ptvv-1g7i-rYawVHOiqHtw")])],"isStart":false});
            var Q9;
            Q9=makeQuery(id+"F1.opExtrude","CAP_EDGE",EDGE,{"disambiguationData":[OSD([sQuery(id+"F0.wireOp",EDGE,"rZGNKk4H-3cCX-Ptvv-1g7i-rYawVHOiqHtw")])],"isStart":true});
            var Q10;
            Q10=makeQuery(id+"F1.opExtrude","SWEPT_EDGE",EDGE,{"disambiguationData":[OSD([sQuery(id+"F0.wireOp",EDGE,"rZGNKk4H-3cCX-Ptvv-1g7i-rYawVHOiqHtw"),sQuery(id+"F0.wireOp",EDGE,"9tkGvgqf-PRiG-9TmJ-UGps-xtPgD0vugzw6")])]});
            var Q11;
            Q11=makeQuery(id+"F1.opExtrude","SWEPT_EDGE",EDGE,{"disambiguationData":[OSD([sQuery(id+"F0.wireOp",EDGE,"E2"),sQuery(id+"F0.wireOp",EDGE,"E275")])]});
            var Q12;
            Q12=makeQuery(id+"F1.opExtrude","CAP_EDGE",EDGE,{"disambiguationData":[OSD([sQuery(id+"F0.wireOp",EDGE,"E283")])],"isStart":true});
            var Q13;
            Q13=makeQuery(id+"F1.opExtrude","CAP_EDGE",EDGE,{"disambiguationData":[OSD([sQuery(id+"F0.wireOp",EDGE,"E283")])],"isStart":false});
            fillet(context, id + "F3", {"entities" : qUnion([Q0, Q1, Q2, Q3, Q4, Q5, Q6, Q7, Q8, Q9, Q10, Q11, Q12, Q13]), "radius" : 2 * mm, "tangentPropagation" : true, "allowEdgeOverflow" : false});
        }
    });
